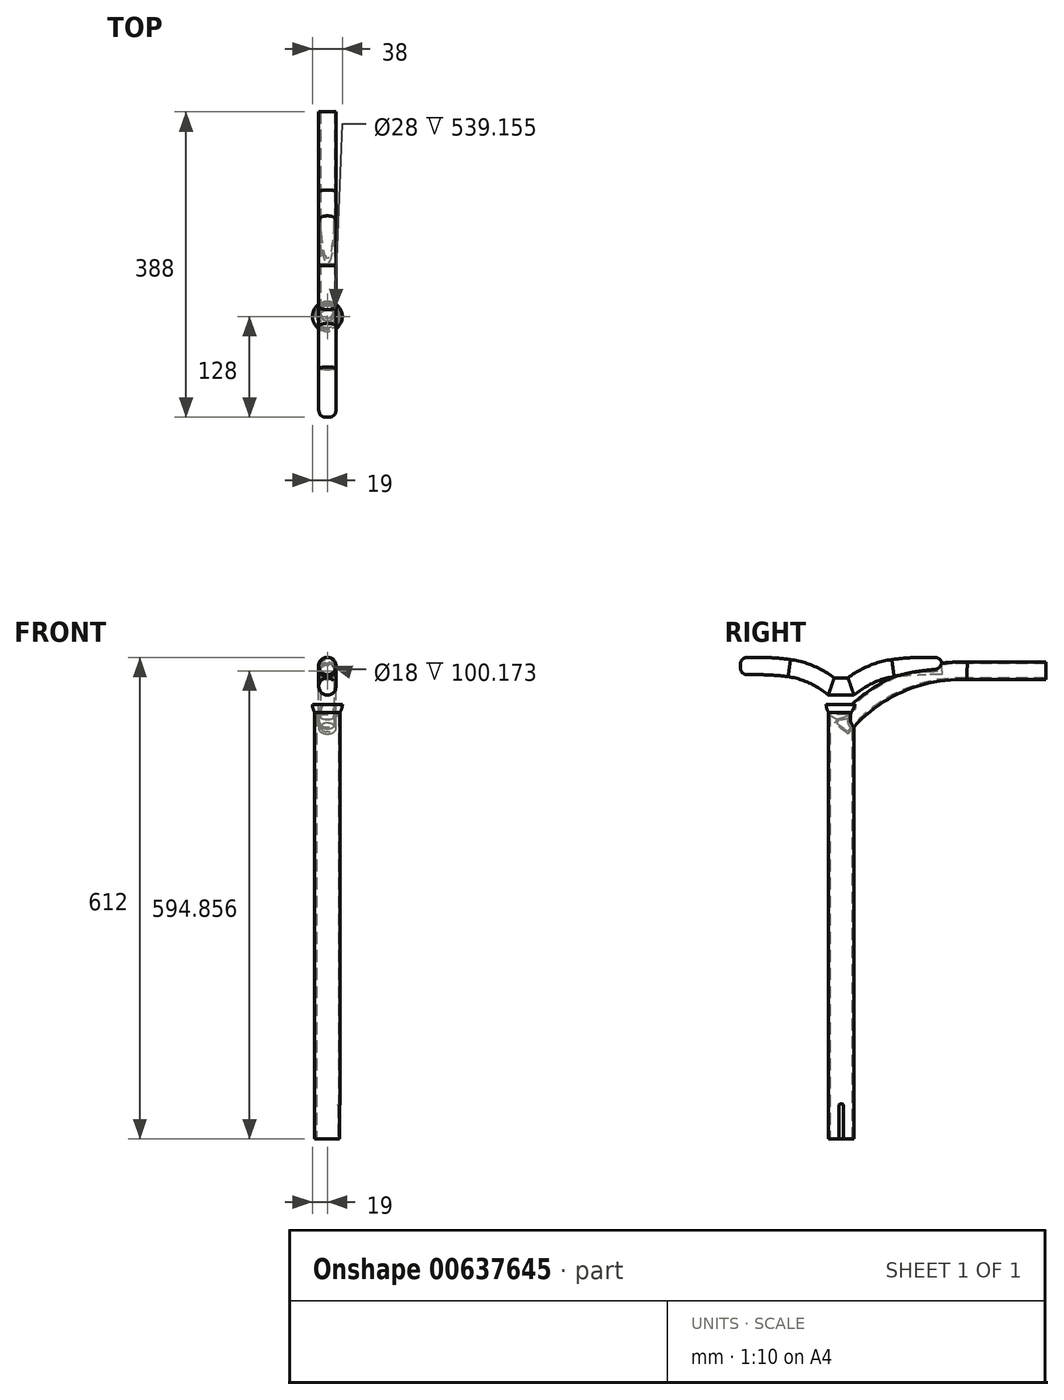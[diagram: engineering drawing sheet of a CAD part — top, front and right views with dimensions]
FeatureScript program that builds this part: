
annotation { "Feature Type Name" : "Feature", "Feature Type Description" : "" }
export const myFeature = defineFeature(function(context is Context, id is Id, definition is map)
    precondition{}
    {
        {
            var Q0;
            Q0=qCreatedBy(makeId("Top.planeOp"),FACE);
            var sketch = newSketch(context, id + "F0", { "sketchPlane" : qUnion([Q0])});
            skCircle(sketch, "E0", {"center": v(0, 0) * mm, "radius": 16 * mm});
            skSolve(sketch);
        }
        {
            var Q0;
            Q0 = qSketchRegion(id + "F0", true);
            extrude(context, id + "F1", {"entities" : qUnion([Q0]), "depth" : 550 * mm, "offsetDistance" : 25 * mm});
        }
        {
            var Q0;
            Q0=makeQuery(id+"F1.opExtrude","CAP_FACE",FACE,{"disambiguationData":[OSD([sQuery(id+"F0.wireOp",EDGE,"E0")])],"isStart":true});
            shell(context, id + "F2", {"entities" : qUnion([Q0]), "thickness" : 2 * mm});
        }
        {
            var Q0;
            Q0=qCreatedBy(makeId("Right.planeOp"),FACE);
            var sketch = newSketch(context, id + "F3", { "sketchPlane" : qUnion([Q0])});
            skLineSegment(sketch, "E1.bottom", {"start": v(0, 45) * mm, "end": v(0, 45) * mm});
            skLineSegment(sketch, "E1.top", {"start": v(-3, 0) * mm, "end": v(3, 0) * mm});
            skLineSegment(sketch, "E1.left", {"start": v(-3, 42) * mm, "end": v(-3, 0) * mm});
            skLineSegment(sketch, "E1.right", {"start": v(3, 42) * mm, "end": v(3, 0) * mm});
            skPoint(sketch, "E2.visualSharp", {"position": v(-3, 45) * mm});
            skArc(sketch, "E2.filletArc", {"start": v(0, 45) * mm, "mid": v(-2.12, 44.12) * mm, "end": v(-3, 42) * mm});
            skPoint(sketch, "E3.visualSharp", {"position": v(3, 45) * mm});
            skArc(sketch, "E3.filletArc", {"start": v(3, 42) * mm, "mid": v(2.12, 44.12) * mm, "end": v(0, 45) * mm});
            skSolve(sketch);
        }
        {
            var Q0;
            Q0 = qSketchRegion(id + "F3", true);
            extrude(context, id + "F4", {"entities" : qUnion([Q0]), "operationType" : NewBodyOperationType.REMOVE, "endBound" : BoundingType.THROUGH_ALL, "depth" : 25 * mm, "offsetDistance" : 25 * mm});
        }
        {
            var Q0;
            Q0=qCreatedBy(makeId("Right.planeOp"),FACE);
            var sketch = newSketch(context, id + "F5", { "sketchPlane" : qUnion([Q0])});
            skArc(sketch, "E4", {"start": v(160, 594.86) * mm, "mid": v(71.26, 577.27) * mm, "end": v(0, 521.53) * mm});
            skLineSegment(sketch, "E5", {"start": v(160, 594.86) * mm, "end": v(260, 594.86) * mm});
            skSolve(sketch);
        }
        {
            var Q0;
            Q0=sQuery(id+"F5.wireOp",VERTEX,"E5.end");
            var Q1;
            Q1=qCreatedBy(makeId("Front.planeOp"),FACE);
            cPlane(context, id + "F6", {"entities" : qUnion([Q0, Q1]), "cplaneType" : CPlaneType.PLANE_POINT, "offset" : 25 * mm, "width" : 150 * mm, "height" : 150 * mm});
        }
        {
            var Q0;
            Q0=qCreatedBy(id+"F6.planeOp",FACE);
            var sketch = newSketch(context, id + "F7", { "sketchPlane" : qUnion([Q0])});
            skCircle(sketch, "E6", {"center": v(0, 594.86) * mm, "radius": 11 * mm});
            skSolve(sketch);
        }
        {
            var Q0;
            Q0=makeQuery(id+"F7.imprint","IMPRINT",FACE,{"disambiguationData":[TD([[makeQuery(id+"F7.imprint","IMPRINT",EDGE,{"derivedFrom":sQuery(id+"F7.wireOp",EDGE,"E6")}),1.0]])]});
            var Q1;
            Q1=sQuery(id+"F5.wireOp",EDGE,"E4");
            var Q2;
            Q2=sQuery(id+"F5.wireOp",EDGE,"E5");
            sweep(context, id + "F8", {"operationType" : NewBodyOperationType.ADD, "profiles" : qUnion([Q0]), "path" : qUnion([Q1, Q2])});
        }
        {
            var Q0;
            Q0=makeQuery(id+"F8.opSweep","CAP_FACE",FACE,{"disambiguationData":[OSD([sQuery(id+"F5.wireOp",VERTEX,"E5.end"),sQuery(id+"F7.wireOp",EDGE,"E6")])],"isStart":true});
            shell(context, id + "F9", {"entities" : qUnion([Q0]), "thickness" : 2 * mm});
        }
        {
            var Q0;
            Q0=qCreatedBy(makeId("Right.planeOp"),FACE);
            var sketch = newSketch(context, id + "F10", { "sketchPlane" : qUnion([Q0])});
            skLineSegment(sketch, "E7", {"start": v(0, 0) * mm, "end": v(0, 575) * mm, "construction": true});
            skLineSegment(sketch, "E8", {"start": v(-128, 601) * mm, "end": v(-108, 601) * mm});
            skArc(sketch, "E9", {"start": v(-65.78, 598.39) * mm, "mid": v(-86.85, 600.35) * mm, "end": v(-108, 601) * mm});
            skLineSegment(sketch, "E10", {"start": v(0, 575) * mm, "end": v(-12.5, 575) * mm});
            skArc(sketch, "E11", {"start": v(-12.5, 575) * mm, "mid": v(-37.6, 590.21) * mm, "end": v(-65.78, 598.39) * mm});
            skLineSegment(sketch, "E12.MirrorCS", {"start": v(0, 575) * mm, "end": v(12.5, 575) * mm});
            skArc(sketch, "E13.MirrorCS", {"start": v(12.5, 575) * mm, "mid": v(37.6, 590.21) * mm, "end": v(65.78, 598.39) * mm});
            skArc(sketch, "E14.MirrorCS", {"start": v(65.78, 598.39) * mm, "mid": v(86.85, 600.35) * mm, "end": v(108, 601) * mm});
            skLineSegment(sketch, "E15.MirrorCS", {"start": v(128, 601) * mm, "end": v(108, 601) * mm});
            skSolve(sketch);
        }
        {
            var Q0;
            Q0=sQuery(id+"F10.wireOp",VERTEX,"E15.MirrorCS.start");
            var Q1;
            Q1=qCreatedBy(id+"F6.planeOp",FACE);
            cPlane(context, id + "F11", {"entities" : qUnion([Q0, Q1]), "cplaneType" : CPlaneType.PLANE_POINT, "offset" : 25 * mm, "width" : 150 * mm, "height" : 150 * mm});
        }
        {
            var Q0;
            Q0=qCreatedBy(id+"F11.planeOp",FACE);
            var sketch = newSketch(context, id + "F12", { "sketchPlane" : qUnion([Q0])});
            skCircle(sketch, "E16", {"center": v(0, 601) * mm, "radius": 11 * mm});
            skSolve(sketch);
        }
        {
            var Q0;
            Q0 = qSketchRegion(id + "F12", true);
            var Q1;
            Q1 = qConstructionFilter(qBodyType(qCreatedBy(id + "F10" ,EDGE), BodyType.WIRE), ConstructionObject.NO);
            sweep(context, id + "F13", {"operationType" : NewBodyOperationType.ADD, "profiles" : qUnion([Q0]), "path" : qUnion([Q1])});
        }
        {
            var Q0;
            Q0=makeQuery(id+"F13.opSweep","CAP_EDGE",EDGE,{"disambiguationData":[OSD([sQuery(id+"F10.wireOp",VERTEX,"E8.start"),sQuery(id+"F12.wireOp",EDGE,"E16")])],"isStart":false});
            var Q1;
            {var subQ0=sQuery(id+"F12.wireOp",EDGE,"E16");var subQ1=sQuery(id+"F10.wireOp",VERTEX,"E15.MirrorCS.start");Q1=makeQuery(id+"F13.boolean.opBoolean","SPLIT",EDGE,{"disambiguationData":[TD([makeQuery(id+"F8.opSweep","SWEPT_FACE",FACE,{"disambiguationData":[OSD([sQuery(id+"F5.wireOp",EDGE,"E4"),sQuery(id+"F7.wireOp",EDGE,"E6")])]})])],"derivedFrom":makeQuery(id+"F13.opSweep","CAP_EDGE",EDGE,{"disambiguationData":[OSD([subQ1,subQ0])],"isStart":true})});}
            fillet(context, id + "F14", {"entities" : qUnion([Q0, Q1]), "radius" : 10 * mm, "tangentPropagation" : true, "rho" : 0.5, "crossSection" : FilletCrossSection.CONIC, "allowEdgeOverflow" : false});
        }
        {
            var Q0;
            Q0=qCreatedBy(makeId("Right.planeOp"),FACE);
            var sketch = newSketch(context, id + "F15", { "sketchPlane" : qUnion([Q0])});
            skArc(sketch, "E17", {"start": v(-19, 552) * mm, "mid": v(-13.44, 538.56) * mm, "end": v(0, 533) * mm});
            skLineSegment(sketch, "E18", {"start": v(-19, 552) * mm, "end": v(0, 552) * mm});
            skLineSegment(sketch, "E19", {"start": v(0, 552) * mm, "end": v(0, 533) * mm});
            skSolve(sketch);
        }
        {
            var Q0;
            Q0 = qSketchRegion(id + "F15", true);
            var Q1;
            Q1=makeQuery(id+"F1.opExtrude","SWEPT_FACE",FACE,{"disambiguationData":[OSD([sQuery(id+"F0.wireOp",EDGE,"E0")])]});
            revolve(context, id + "F16", {"operationType" : NewBodyOperationType.ADD, "surfaceOperationType" : NewSurfaceOperationType.NEW, "entities" : qUnion([Q0]), "axis" : qUnion([Q1]), "revolveType" : RevolveType.FULL});
        }
    });
